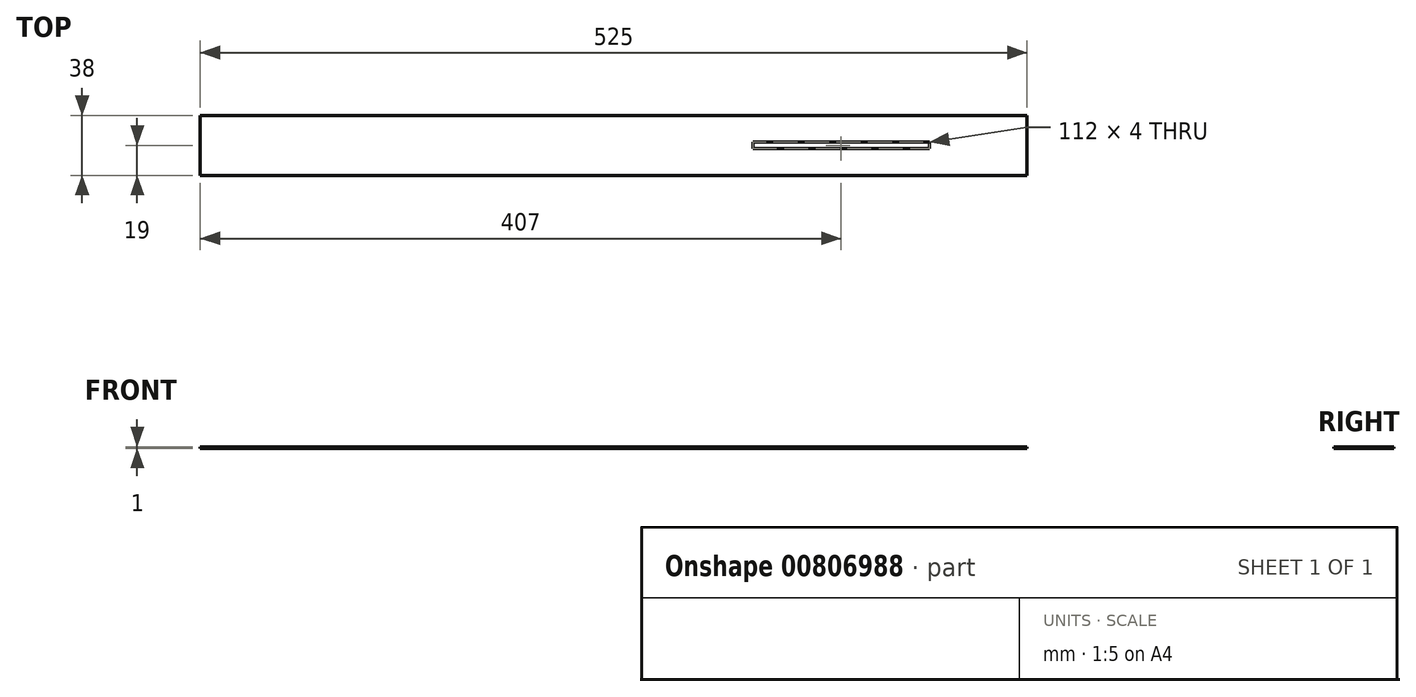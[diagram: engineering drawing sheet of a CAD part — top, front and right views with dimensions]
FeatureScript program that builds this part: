
annotation { "Feature Type Name" : "Feature", "Feature Type Description" : "" }
export const myFeature = defineFeature(function(context is Context, id is Id, definition is map)
    precondition{}
    {
        {
            var Q0;
            Q0=qCreatedBy(makeId("Top.planeOp"),FACE);
            var sketch = newSketch(context, id + "F0", { "sketchPlane" : qUnion([Q0])});
            skLineSegment(sketch, "E0.bottom", {"start": v(-263, 19) * mm, "end": v(262, 19) * mm});
            skLineSegment(sketch, "E0.top", {"start": v(-263, -19) * mm, "end": v(262, -19) * mm});
            skLineSegment(sketch, "E0.left", {"start": v(-263, 19) * mm, "end": v(-263, -19) * mm});
            skLineSegment(sketch, "E0.right", {"start": v(262, 19) * mm, "end": v(262, -19) * mm});
            skSolve(sketch);
        }
        {
            var Q0;
            Q0=makeQuery(id+"F0.imprint","IMPRINT",FACE,{"disambiguationData":[TD([[makeQuery(id+"F0.imprint","IMPRINT",EDGE,{"derivedFrom":sQuery(id+"F0.wireOp",EDGE,"E0.bottom")}),-1.0]])]});
            extrude(context, id + "F1", {"entities" : qUnion([Q0]), "depth" : 1 * mm});
        }
        {
            var Q0;
            Q0=makeQuery(id+"F1.opExtrude","CAP_FACE",FACE,{"disambiguationData":[OSD([sQuery(id+"F0.wireOp",EDGE,"E0.bottom"),sQuery(id+"F0.wireOp",EDGE,"E0.top"),sQuery(id+"F0.wireOp",EDGE,"E0.left"),sQuery(id+"F0.wireOp",EDGE,"E0.right")])],"isStart":false});
            var sketch = newSketch(context, id + "F2", { "sketchPlane" : qUnion([Q0])});
            skLineSegment(sketch, "E1.bottom", {"start": v(88, 2) * mm, "end": v(200, 2) * mm});
            skLineSegment(sketch, "E1.top", {"start": v(88, -2) * mm, "end": v(200, -2) * mm});
            skLineSegment(sketch, "E1.left", {"start": v(88, 2) * mm, "end": v(88, -2) * mm});
            skLineSegment(sketch, "E1.right", {"start": v(200, 2) * mm, "end": v(200, -2) * mm});
            skSolve(sketch);
        }
        {
            var Q0;
            Q0=makeQuery(id+"F2.imprint","IMPRINT",FACE,{"disambiguationData":[TD([[makeQuery(id+"F2.imprint","IMPRINT",EDGE,{"derivedFrom":sQuery(id+"F2.wireOp",EDGE,"E1.bottom")}),-1.0]])]});
            extrude(context, id + "F3", {"entities" : qUnion([Q0]), "operationType" : NewBodyOperationType.REMOVE, "oppositeDirection" : true, "depth" : 1 * mm, "offsetDistance" : 25 * mm});
        }
    });
